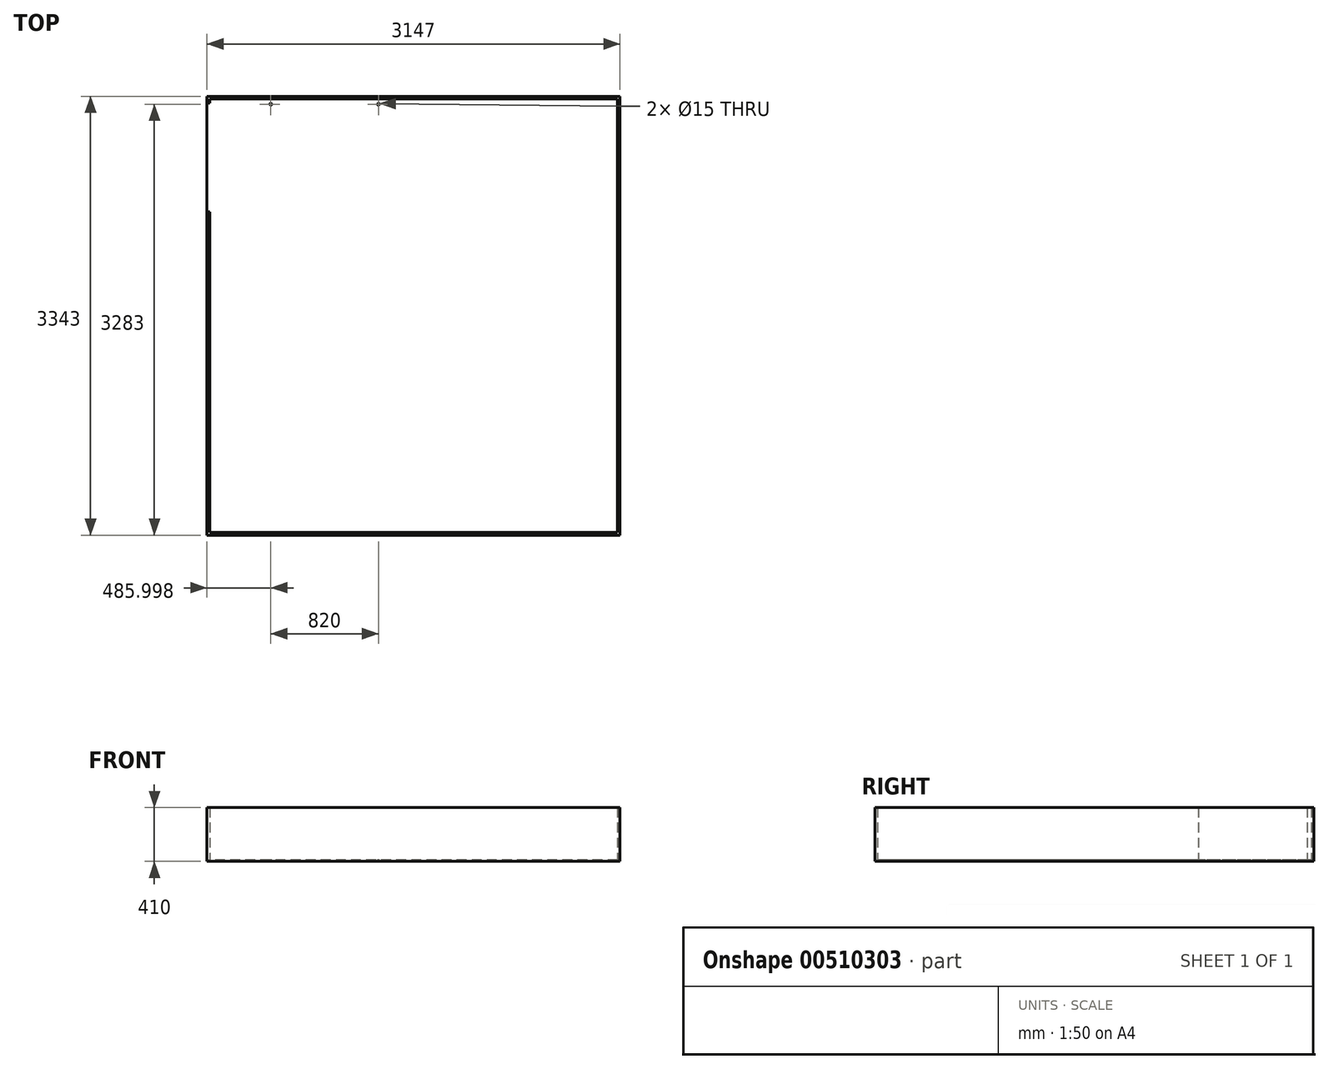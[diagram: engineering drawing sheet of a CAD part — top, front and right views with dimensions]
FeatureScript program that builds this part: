
annotation { "Feature Type Name" : "Feature", "Feature Type Description" : "" }
export const myFeature = defineFeature(function(context is Context, id is Id, definition is map)
    precondition{}
    {
        {
            var Q0;
            Q0=qCreatedBy(makeId("Top.planeOp"),FACE);
            var sketch = newSketch(context, id + "F0", { "sketchPlane" : qUnion([Q0])});
            skLineSegment(sketch, "E0", {"start": v(-1153.1, 305.24) * mm, "end": v(-1153.1, -3037.76) * mm});
            skLineSegment(sketch, "E1", {"start": v(-1153.1, 305.24) * mm, "end": v(1993.9, 305.24) * mm});
            skLineSegment(sketch, "E2", {"start": v(1993.9, 305.24) * mm, "end": v(1993.9, -3037.76) * mm});
            skLineSegment(sketch, "E3", {"start": v(1993.9, -3037.76) * mm, "end": v(-1153.1, -3037.76) * mm});
            skSolve(sketch);
        }
        {
            var Q0;
            Q0=qSketchRegion(id+"F0",true);
            extrude(context, id + "F1", {"entities" : qUnion([Q0]), "depth" : 10 * mm});
        }
        {
            var Q0;
            Q0=makeQuery(id+"F1.opExtrude","CAP_FACE",FACE,{"disambiguationData":[OSD([sQuery(id+"F0.wireOp",EDGE,"E0"),sQuery(id+"F0.wireOp",EDGE,"E1"),sQuery(id+"F0.wireOp",EDGE,"WgVKCl0m-d2Fn-ZN4z-6Op2-v5l7jUpCpKGt"),sQuery(id+"F0.wireOp",EDGE,"wwQjYG4k-yRsa-x1RV-Ti9H-1UnRLhNkFOyi"),sQuery(id+"F0.wireOp",EDGE,"E2"),sQuery(id+"F0.wireOp",EDGE,"E3")])],"isStart":false});
            var sketch = newSketch(context, id + "F2", { "sketchPlane" : qUnion([Q0])});
            skLineSegment(sketch, "E4.top", {"start": v(-1153.1, 255.24) * mm, "end": v(-1133.1, 255.24) * mm});
            skLineSegment(sketch, "E4.left", {"start": v(-1153.1, 305.24) * mm, "end": v(-1153.1, 255.24) * mm});
            skLineSegment(sketch, "E4.right", {"start": v(-1133.1, 285.24) * mm, "end": v(-1133.1, 255.24) * mm});
            skLineSegment(sketch, "E5.bottom", {"start": v(-1153.1, 305.24) * mm, "end": v(1993.9, 305.24) * mm});
            skLineSegment(sketch, "E5.top", {"start": v(-1133.1, 285.24) * mm, "end": v(1973.9, 285.24) * mm});
            skLineSegment(sketch, "E6.right", {"start": v(1973.9, 285.24) * mm, "end": v(1973.9, -3017.76) * mm});
            skLineSegment(sketch, "E7.top", {"start": v(1973.9, -3017.76) * mm, "end": v(-1133.1, -3017.76) * mm});
            skLineSegment(sketch, "E8", {"start": v(1993.9, 305.24) * mm, "end": v(1993.9, -3037.76) * mm});
            skLineSegment(sketch, "E9", {"start": v(1993.9, -3037.76) * mm, "end": v(-1153.1, -3037.76) * mm});
            skLineSegment(sketch, "E10", {"start": v(-1153.1, -3037.76) * mm, "end": v(-1153.1, -574.76) * mm});
            skLineSegment(sketch, "E11", {"start": v(-1153.1, -574.76) * mm, "end": v(-1133.1, -574.76) * mm});
            skLineSegment(sketch, "E12", {"start": v(-1133.1, -574.76) * mm, "end": v(-1133.1, -3017.76) * mm});
            skSolve(sketch);
        }
        {
            var Q0;
            Q0=makeQuery(id+"F2.imprint","IMPRINT",FACE,{"disambiguationData":[TD([[makeQuery(id+"F2.imprint","IMPRINT",EDGE,{"derivedFrom":sQuery(id+"F2.wireOp",EDGE,"E4.top")}),1.0]])]});
            var Q1;
            Q1=makeQuery(id+"F2.imprint","IMPRINT",FACE,{"disambiguationData":[TD([[makeQuery(id+"F2.imprint","IMPRINT",EDGE,{"derivedFrom":sQuery(id+"F2.wireOp",EDGE,"E6.right")}),1.0]])]});
            extrude(context, id + "F3", {"entities" : qUnion([Q0, Q1]), "operationType" : NewBodyOperationType.ADD, "depth" : 400 * mm});
        }
        {
            var Q0;
            Q0=makeQuery(id+"F1.opExtrude","CAP_FACE",FACE,{"disambiguationData":[OSD([sQuery(id+"F0.wireOp",EDGE,"E0"),sQuery(id+"F0.wireOp",EDGE,"E1"),sQuery(id+"F0.wireOp",EDGE,"WgVKCl0m-d2Fn-ZN4z-6Op2-v5l7jUpCpKGt"),sQuery(id+"F0.wireOp",EDGE,"wwQjYG4k-yRsa-x1RV-Ti9H-1UnRLhNkFOyi"),sQuery(id+"F0.wireOp",EDGE,"E2"),sQuery(id+"F0.wireOp",EDGE,"E3")])],"isStart":false});
            var sketch = newSketch(context, id + "F4", { "sketchPlane" : qUnion([Q0])});
            skCircle(sketch, "E13", {"center": v(-667.1, 245.24) * mm, "radius": 7.5 * mm});
            skCircle(sketch, "E14", {"center": v(152.9, 245.24) * mm, "radius": 7.5 * mm});
            skSolve(sketch);
        }
        {
            var Q0;
            Q0=qSketchRegion(id+"F4",true);
            extrude(context, id + "F5", {"entities" : qUnion([Q0]), "operationType" : NewBodyOperationType.REMOVE, "oppositeDirection" : true, "depth" : 25 * mm});
        }
    });
